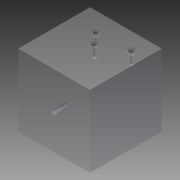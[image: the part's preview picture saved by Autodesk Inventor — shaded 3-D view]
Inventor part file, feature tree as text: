
AUTODESK INVENTOR PART (.ipt)
format: ipt  version: 2014 (Build 180170000, 170)  size: 261,632 bytes
history: native  units: mm
features: other x54, sketch x11, extrude x4
ambient origin geometry x8: Origin, YZ Plane, XZ Plane, XY Plane, X Axis, Y Axis, Z Axis, Center Point
bodies: 实体1 (feature_tree)
feature tree (69):
  extrude  "拉伸1"  TaperAngle=0.0deg  [1 undecoded]
  other  "UCS1"
  other  "UCS2"
  other  "UCS3"
  other  "UCS4"
  other  "UCS5"
  other  "UCS6"
  sketch  "草图1"  dims[d0=300.0mm d1=0.0mm]
  sketch  "草图3"  dims[d8=0.0mm d9=0.0mm d10=0.0mm d11=0.0mm d12=0.0mm d13=0.0mm]
  other  "曲面1"
  sketch  "草图4"  dims[d14=0.0mm d15=0.0mm d16=0.0mm d17=0.0mm d18=0.0mm d19=0.0mm]
  other  "曲面2"
  sketch  "草图6"  dims[d26=0.0mm d27=0.0mm d28=0.0mm d29=0.0mm d30=0.0mm d31=0.0mm]
  other  "曲面3"
  sketch  "草图8"  dims[d42=-31.29mm d43=0.13mm d44=0.0mm]
  other  "曲面4"
  sketch  "草图10"  dims[d48=0.0mm d52=-13.99mm]
  other  "曲面5"
  sketch  "草图11"  dims[d53=0.13mm d54=0.0mm d55=0.0mm d59=-13.49mm d60=0.13mm d61=0.0mm d62=0.0mm d66=-31.29mm d67=0.13mm d68=0.0mm d69=-17.79mm d70=5.0mm d71=0.0mm]
  other  "曲面6"
  extrude  "拉伸曲面1"  Depth=0.13mm TaperAngle=0.0deg
  extrude  "拉伸曲面2"  Depth=5.0mm TaperAngle=0.0deg
  extrude  "拉伸曲面3"  [1 undecoded]
  other  "UCS1: YZ 平面"
  other  "UCS1: XZ 平面"
  other  "UCS1: XY 平面"
  other  "UCS1: X 轴"
  other  "UCS1: Y 轴"
  other  "UCS1: Z 轴"
  other  "UCS1: 原点"
  other  "UCS2: YZ 平面"
  other  "UCS2: XZ 平面"
  other  "UCS2: XY 平面"
  other  "UCS2: X 轴"
  other  "UCS2: Y 轴"
  other  "UCS2: Z 轴"
  other  "UCS2: 原点"
  other  "UCS3: YZ 平面"
  other  "UCS3: XZ 平面"
  other  "UCS3: XY 平面"
  other  "UCS3: X 轴"
  other  "UCS3: Y 轴"
  other  "UCS3: Z 轴"
  other  "UCS3: 原点"
  other  "UCS4: YZ 平面"
  other  "UCS4: XZ 平面"
  other  "UCS4: XY 平面"
  other  "UCS4: X 轴"
  other  "UCS4: Y 轴"
  other  "UCS4: Z 轴"
  other  "UCS4: 原点"
  other  "UCS5: YZ 平面"
  other  "UCS5: XZ 平面"
  other  "UCS5: XY 平面"
  other  "UCS5: X 轴"
  other  "UCS5: Y 轴"
  other  "UCS5: Z 轴"
  other  "UCS5: 原点"
  other  "UCS6: YZ 平面"
  other  "UCS6: XZ 平面"
  other  "UCS6: XY 平面"
  other  "UCS6: X 轴"
  other  "UCS6: Y 轴"
  other  "UCS6: Z 轴"
  other  "UCS6: 原点"
  sketch  "草图2"  dims[d2=0.0mm d3=0.0mm d4=0.0mm d5=0.0mm d6=0.0mm d7=0.0mm]
  sketch  "草图5"  dims[d20=0.0mm d21=0.0mm d22=0.0mm d23=0.0mm d24=0.0mm d25=0.0mm]
  sketch  "草图7"  dims[d32=0.0mm d33=0.0mm d34=0.0mm d35=0.0mm d36=0.0mm d37=0.0mm d38=0.0mm]
  sketch  "草图9"  dims[d45=-17.79mm d46=5.0mm d47=0.0mm]
note: 2 required parameter values undecoded (feature->parameter linkage not recoverable at this tier; creation-order binding heuristic only, values carry confidence <= 0.55)
